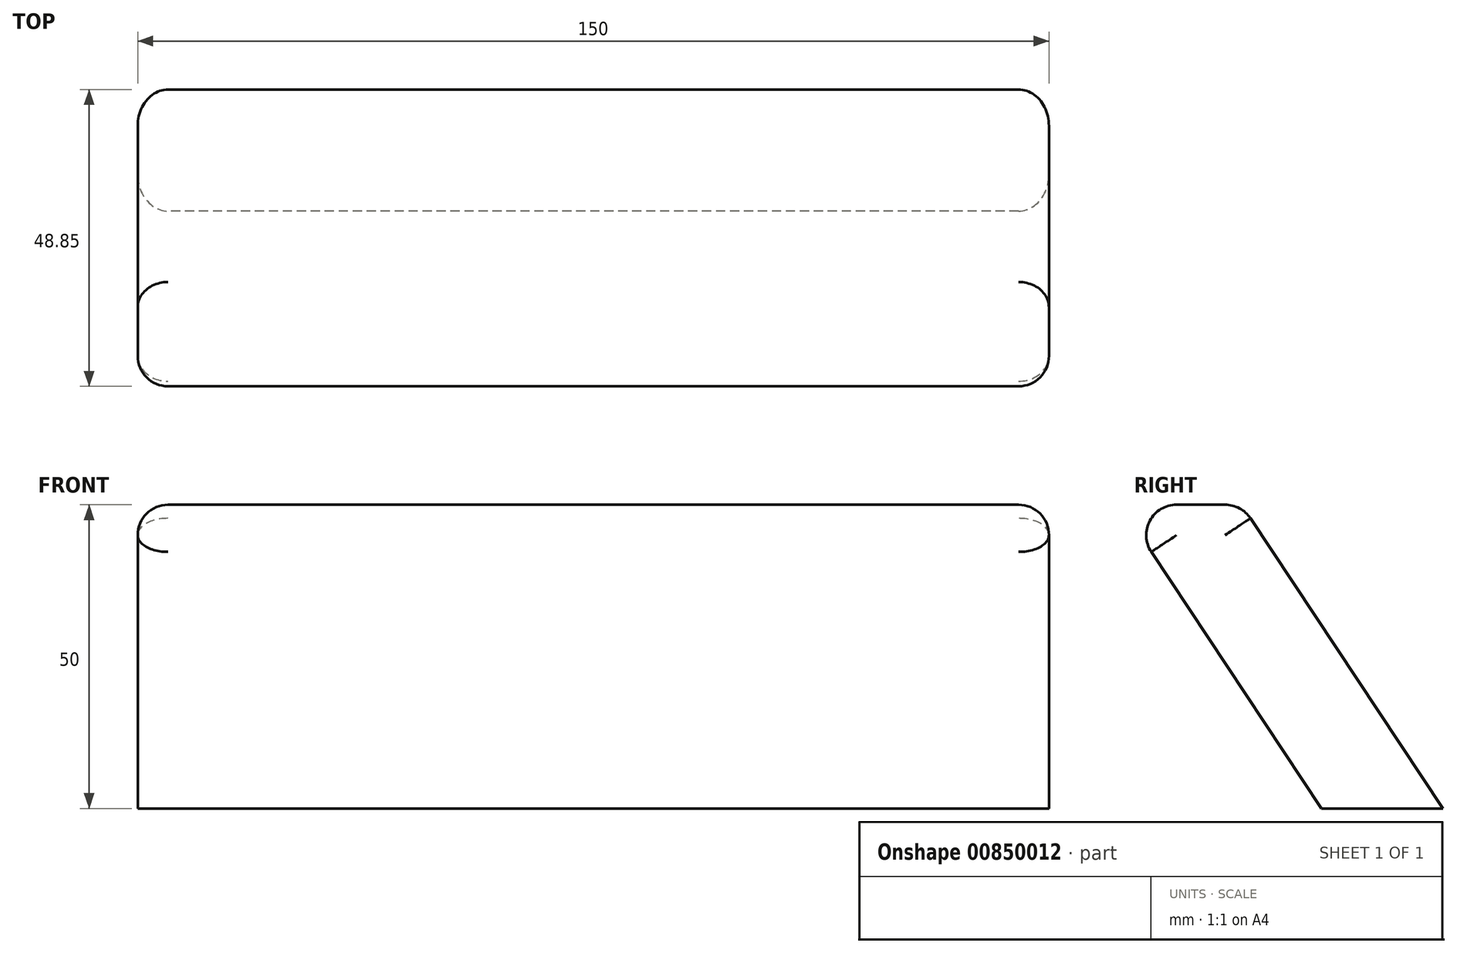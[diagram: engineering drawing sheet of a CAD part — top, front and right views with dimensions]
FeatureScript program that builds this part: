
annotation { "Feature Type Name" : "Feature", "Feature Type Description" : "" }
export const myFeature = defineFeature(function(context is Context, id is Id, definition is map)
    precondition{}
    {
        {
            var Q0;
            Q0=qCreatedBy(makeId("Right.planeOp"),FACE);
            var sketch = newSketch(context, id + "F0", { "sketchPlane" : qUnion([Q0])});
            skLineSegment(sketch, "E0", {"start": v(17.91, 0) * mm, "end": v(37.91, 0) * mm});
            skLineSegment(sketch, "E1", {"start": v(4.75, 50) * mm, "end": v(-15.25, 50) * mm});
            skLineSegment(sketch, "E2", {"start": v(4.75, 50) * mm, "end": v(37.91, 0) * mm});
            skLineSegment(sketch, "E3", {"start": v(-15.25, 50) * mm, "end": v(17.91, 0) * mm});
            skSolve(sketch);
        }
        {
            var Q0;
            Q0=makeQuery(id+"F0.imprint","IMPRINT",FACE,{"disambiguationData":[TD([[makeQuery(id+"F0.imprint","IMPRINT",EDGE,{"derivedFrom":sQuery(id+"F0.wireOp",EDGE,"E0")}),1.0]])]});
            extrude(context, id + "F1", {"entities" : qUnion([Q0]), "endBound" : BoundingType.SYMMETRIC, "depth" : 150 * mm, "offsetDistance" : 25 * mm});
        }
        {
            var Q0;
            Q0=makeQuery(id+"F1.opExtrude","SWEPT_FACE",FACE,{"disambiguationData":[OSD([sQuery(id+"F0.wireOp",EDGE,"E1")])]});
            fillet(context, id + "F2", {"entities" : qUnion([Q0]), "radius" : 5 * mm, "tangentPropagation" : true, "allowEdgeOverflow" : false});
        }
        {
            var Q0;
            Q0=makeQuery(id+"F1.opExtrude","CAP_EDGE",EDGE,{"disambiguationData":[OSD([sQuery(id+"F0.wireOp",EDGE,"E2")])],"isStart":false});
            var Q1;
            Q1=makeQuery(id+"F1.opExtrude","CAP_EDGE",EDGE,{"disambiguationData":[OSD([sQuery(id+"F0.wireOp",EDGE,"E2")])],"isStart":true});
            var Q2;
            Q2=makeQuery(id+"F1.opExtrude","CAP_EDGE",EDGE,{"disambiguationData":[OSD([sQuery(id+"F0.wireOp",EDGE,"E3")])],"isStart":false});
            var Q3;
            Q3=makeQuery(id+"F1.opExtrude","CAP_EDGE",EDGE,{"disambiguationData":[OSD([sQuery(id+"F0.wireOp",EDGE,"E3")])],"isStart":true});
            fillet(context, id + "F3", {"entities" : qUnion([Q0, Q1, Q2, Q3]), "radius" : 5 * mm, "tangentPropagation" : true, "allowEdgeOverflow" : false});
        }
    });
